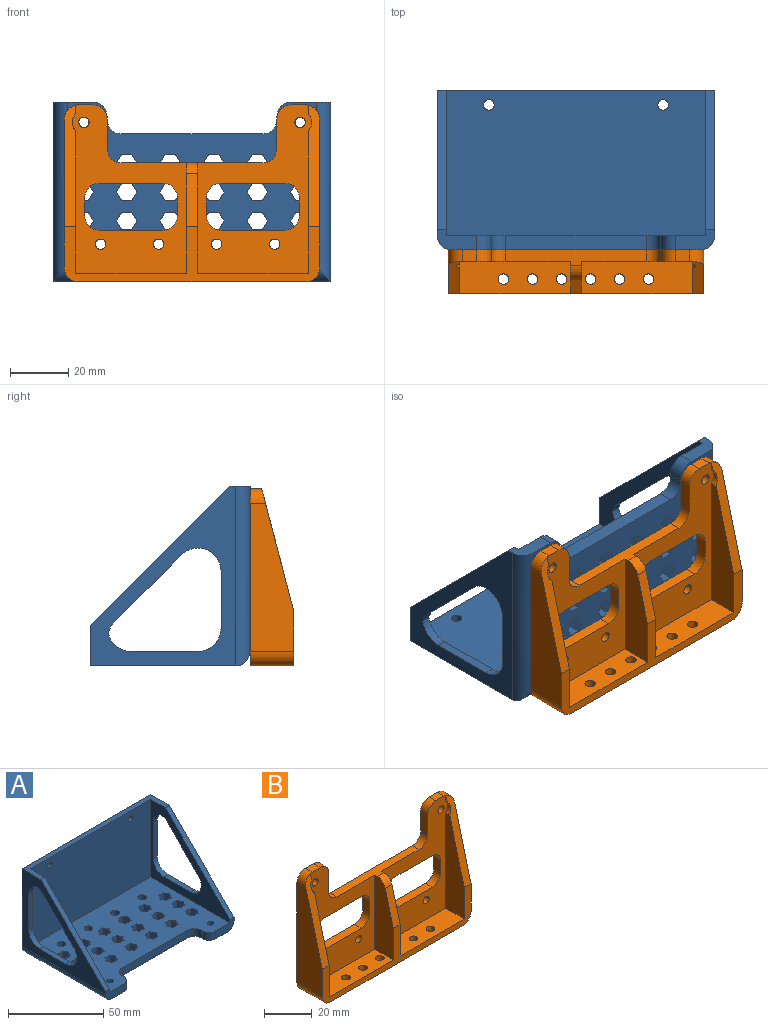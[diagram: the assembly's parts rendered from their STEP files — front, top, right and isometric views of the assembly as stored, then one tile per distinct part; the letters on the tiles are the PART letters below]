
ASSEMBLY  parts=2 mates=1
PART A: 153 faces, bbox 95.5x62x55 mm
  f0: plane 62x50mm, normal (1,0,0), area 986mm2, adj f6,f7,f15,f20,f28,f139,f140,f141
  f1: plane 62x50mm, normal (-1,0,0), area 986mm2, adj f7,f8,f15,f21,f30,f142,f143,f144
  f2: plane 59x50mm, normal (1,0,0), area 836mm2, adj f8,f12,f14,f15,f21,f142,f143,f144
  f3: plane 59x50mm, normal (-1,0,0), area 836mm2, adj f6,f12,f14,f15,f20,f139,f140,f141
  f4: plane 48.5x5mm, normal (0,-1,0), area 242.5mm2, adj f12,f13,f22,f23
  f5: plane 5x1mm, normal (-1,0,0), area 5mm2, adj f12,f13,f22,f25
  f6: plane 13.5x7mm, normal (0,-1,0), area 68.1mm2, adj f0,f3,f12,f13,f20,f25,f28
  f7: plane 95.5x50mm, normal (0,1,0), area 4754.6mm2, adj f0,f1,f15,f26,f27,f29
  f8: plane 13.5x7mm, normal (0,-1,0), area 68.1mm2, adj f1,f2,f12,f13,f21,f24,f30
  f9: cylinder r=1.75mm len=5mm, axis (0,0,-1), area 55mm2, adj f12,f13
  f10: plane 5x1mm, normal (1,0,0), area 5mm2, adj f12,f13,f23,f24
  f11: cylinder r=1.75mm len=5mm, axis (0,0,-1), area 55mm2, adj f12,f13
  f12: plane 89.5x59mm, normal (0,0,1), area 3993mm2, adj f2,f3,f4,f5,f6,f8,f9,f10
  f13: plane 85.5x57mm, normal (0,0,-1), area 3586mm2, adj f4,f5,f6,f8,f9,f10,f11,f16
  f14: plane 89.5x50mm, normal (0,-1,0), area 4454.6mm2, adj f2,f3,f12,f15,f26,f27
  f15: plane 95.5x14mm, normal (0,0,1), area 352.5mm2, adj f0,f1,f2,f3,f7,f14,f20,f21
  f16: cylinder r=2.25mm len=5mm, axis (0,0,-1), area 70.7mm2, adj f12,f13
  f17: cylinder r=2.25mm len=5mm, axis (0,0,-1), area 70.7mm2, adj f12,f13
  f18: cylinder r=2.25mm len=5mm, axis (0,0,-1), area 70.7mm2, adj f12,f13
  f19: cylinder r=2.25mm len=5mm, axis (0,0,-1), area 70.7mm2, adj f12,f13
  f20: plane 48x48mm, normal (0,-0.71,0.71), area 203.6mm2, adj f0,f3,f6,f15
  f21: plane 48x48mm, normal (0,-0.71,0.71), area 203.6mm2, adj f1,f2,f8,f15
  f22: cylinder r=5mm len=5mm, axis (0,0,-1), area 39.3mm2, adj f4,f5,f12,f13
  f23: cylinder r=5mm len=5mm, axis (0,0,1), area 39.3mm2, adj f4,f10,f12,f13
  f24: cylinder r=5mm len=5mm, axis (0,0,1), area 39.3mm2, adj f8,f10,f12,f13
  f25: cylinder r=5mm len=5mm, axis (0,0,1), area 39.3mm2, adj f5,f6,f12,f13
  f26: cylinder r=1.8mm len=3.6mm, axis (0,-1,0), area 33.9mm2, adj f7,f14
  f27: cylinder r=1.8mm len=3.6mm, axis (0,-1,0), area 33.9mm2, adj f7,f14
  f28: cylinder r=5mm len=62mm, axis (0,1,0), area 472.7mm2, adj f0,f6,f13,f29
  f29: cylinder r=5mm len=95.5mm, axis (-1,0,0), area 721.5mm2, adj f7,f13,f28,f30
  f30: cylinder r=5mm len=62mm, axis (0,-1,0), area 472.7mm2, adj f1,f8,f13,f29
  f31: plane 5x3mm, normal (0.87,-0.5,0), area 17.3mm2, adj f12,f13,f32,f36
  f32: plane 5x3mm, normal (0.87,0.5,0), area 17.3mm2, adj f12,f13,f31,f33
  f33: plane 5x3.46mm, normal (0,1,0), area 17.3mm2, adj f12,f13,f32,f34
  f34: plane 5x3mm, normal (-0.87,0.5,0), area 17.3mm2, adj f12,f13,f33,f35
  f35: plane 5x3mm, normal (-0.87,-0.5,0), area 17.3mm2, adj f12,f13,f34,f36
  f36: plane 5x3.46mm, normal (0,-1,0), area 17.3mm2, adj f12,f13,f31,f35
  f37: plane 5x3mm, normal (0.87,0.5,0), area 17.3mm2, adj f12,f13,f38,f42
  f38: plane 5x3.46mm, normal (0,1,0), area 17.3mm2, adj f12,f13,f37,f39
  f39: plane 5x3mm, normal (-0.87,0.5,0), area 17.3mm2, adj f12,f13,f38,f40
  f40: plane 5x3mm, normal (-0.87,-0.5,0), area 17.3mm2, adj f12,f13,f39,f41
  f41: plane 5x3.46mm, normal (0,-1,0), area 17.3mm2, adj f12,f13,f40,f42
  f42: plane 5x3mm, normal (0.87,-0.5,0), area 17.3mm2, adj f12,f13,f37,f41
  f43: plane 5x3mm, normal (0.87,0.5,0), area 17.3mm2, adj f12,f13,f44,f48
  f44: plane 5x3.46mm, normal (0,1,0), area 17.3mm2, adj f12,f13,f43,f45
  f45: plane 5x3mm, normal (-0.87,0.5,0), area 17.3mm2, adj f12,f13,f44,f46
  f46: plane 5x3mm, normal (-0.87,-0.5,0), area 17.3mm2, adj f12,f13,f45,f47
  f47: plane 5x3.46mm, normal (0,-1,0), area 17.3mm2, adj f12,f13,f46,f48
  f48: plane 5x3mm, normal (0.87,-0.5,0), area 17.3mm2, adj f12,f13,f43,f47
  f49: plane 5x3mm, normal (0.87,0.5,0), area 17.3mm2, adj f12,f13,f50,f54
  f50: plane 5x3.46mm, normal (0,1,0), area 17.3mm2, adj f12,f13,f49,f51
  f51: plane 5x3mm, normal (-0.87,0.5,0), area 17.3mm2, adj f12,f13,f50,f52
  f52: plane 5x3mm, normal (-0.87,-0.5,0), area 17.3mm2, adj f12,f13,f51,f53
  f53: plane 5x3.46mm, normal (0,-1,0), area 17.3mm2, adj f12,f13,f52,f54
  f54: plane 5x3mm, normal (0.87,-0.5,0), area 17.3mm2, adj f12,f13,f49,f53
  f55: plane 5x3mm, normal (0.87,0.5,0), area 17.3mm2, adj f12,f13,f56,f60
  f56: plane 5x3.46mm, normal (0,1,0), area 17.3mm2, adj f12,f13,f55,f57
  f57: plane 5x3mm, normal (-0.87,0.5,0), area 17.3mm2, adj f12,f13,f56,f58
  f58: plane 5x3mm, normal (-0.87,-0.5,0), area 17.3mm2, adj f12,f13,f57,f59
  f59: plane 5x3.46mm, normal (0,-1,0), area 17.3mm2, adj f12,f13,f58,f60
  f60: plane 5x3mm, normal (0.87,-0.5,0), area 17.3mm2, adj f12,f13,f55,f59
  f61: plane 5x3mm, normal (0.87,0.5,0), area 17.3mm2, adj f12,f13,f62,f66
  f62: plane 5x3.46mm, normal (0,1,0), area 17.3mm2, adj f12,f13,f61,f63
  f63: plane 5x3mm, normal (-0.87,0.5,0), area 17.3mm2, adj f12,f13,f62,f64
  f64: plane 5x3mm, normal (-0.87,-0.5,0), area 17.3mm2, adj f12,f13,f63,f65
  f65: plane 5x3.46mm, normal (0,-1,0), area 17.3mm2, adj f12,f13,f64,f66
  f66: plane 5x3mm, normal (0.87,-0.5,0), area 17.3mm2, adj f12,f13,f61,f65
  f67: plane 5x3mm, normal (0.87,0.5,0), area 17.3mm2, adj f12,f13,f68,f72
  f68: plane 5x3.46mm, normal (0,1,0), area 17.3mm2, adj f12,f13,f67,f69
  f69: plane 5x3mm, normal (-0.87,0.5,0), area 17.3mm2, adj f12,f13,f68,f70
  f70: plane 5x3mm, normal (-0.87,-0.5,0), area 17.3mm2, adj f12,f13,f69,f71
  f71: plane 5x3.46mm, normal (0,-1,0), area 17.3mm2, adj f12,f13,f70,f72
  f72: plane 5x3mm, normal (0.87,-0.5,0), area 17.3mm2, adj f12,f13,f67,f71
  f73: plane 5x3mm, normal (0.87,0.5,0), area 17.3mm2, adj f12,f13,f74,f78
  f74: plane 5x3.46mm, normal (0,1,0), area 17.3mm2, adj f12,f13,f73,f75
  f75: plane 5x3mm, normal (-0.87,0.5,0), area 17.3mm2, adj f12,f13,f74,f76
  f76: plane 5x3mm, normal (-0.87,-0.5,0), area 17.3mm2, adj f12,f13,f75,f77
  f77: plane 5x3.46mm, normal (0,-1,0), area 17.3mm2, adj f12,f13,f76,f78
  f78: plane 5x3mm, normal (0.87,-0.5,0), area 17.3mm2, adj f12,f13,f73,f77
  f79: plane 5x3mm, normal (0.87,0.5,0), area 17.3mm2, adj f12,f13,f80,f84
  f80: plane 5x3.46mm, normal (0,1,0), area 17.3mm2, adj f12,f13,f79,f81
  f81: plane 5x3mm, normal (-0.87,0.5,0), area 17.3mm2, adj f12,f13,f80,f82
  f82: plane 5x3mm, normal (-0.87,-0.5,0), area 17.3mm2, adj f12,f13,f81,f83
  f83: plane 5x3.46mm, normal (0,-1,0), area 17.3mm2, adj f12,f13,f82,f84
  f84: plane 5x3mm, normal (0.87,-0.5,0), area 17.3mm2, adj f12,f13,f79,f83
  f85: plane 5x3mm, normal (0.87,0.5,0), area 17.3mm2, adj f12,f13,f86,f90
  f86: plane 5x3.46mm, normal (0,1,0), area 17.3mm2, adj f12,f13,f85,f87
  f87: plane 5x3mm, normal (-0.87,0.5,0), area 17.3mm2, adj f12,f13,f86,f88
  f88: plane 5x3mm, normal (-0.87,-0.5,0), area 17.3mm2, adj f12,f13,f87,f89
  f89: plane 5x3.46mm, normal (0,-1,0), area 17.3mm2, adj f12,f13,f88,f90
  f90: plane 5x3mm, normal (0.87,-0.5,0), area 17.3mm2, adj f12,f13,f85,f89
  f91: plane 5x3mm, normal (0.87,0.5,0), area 17.3mm2, adj f12,f13,f92,f96
  f92: plane 5x3.46mm, normal (0,1,0), area 17.3mm2, adj f12,f13,f91,f93
  f93: plane 5x3mm, normal (-0.87,0.5,0), area 17.3mm2, adj f12,f13,f92,f94
  f94: plane 5x3mm, normal (-0.87,-0.5,0), area 17.3mm2, adj f12,f13,f93,f95
  f95: plane 5x3.46mm, normal (0,-1,0), area 17.3mm2, adj f12,f13,f94,f96
  f96: plane 5x3mm, normal (0.87,-0.5,0), area 17.3mm2, adj f12,f13,f91,f95
  f97: plane 5x3mm, normal (0.87,0.5,0), area 17.3mm2, adj f12,f13,f98,f102
  f98: plane 5x3.46mm, normal (0,1,0), area 17.3mm2, adj f12,f13,f97,f99
  f99: plane 5x3mm, normal (-0.87,0.5,0), area 17.3mm2, adj f12,f13,f98,f100
  f100: plane 5x3mm, normal (-0.87,-0.5,0), area 17.3mm2, adj f12,f13,f99,f101
  f101: plane 5x3.46mm, normal (0,-1,0), area 17.3mm2, adj f12,f13,f100,f102
  f102: plane 5x3mm, normal (0.87,-0.5,0), area 17.3mm2, adj f12,f13,f97,f101
  f103: plane 5x3mm, normal (0.87,0.5,0), area 17.3mm2, adj f12,f13,f104,f108
  f104: plane 5x3.46mm, normal (0,1,0), area 17.3mm2, adj f12,f13,f103,f105
  f105: plane 5x3mm, normal (-0.87,0.5,0), area 17.3mm2, adj f12,f13,f104,f106
  f106: plane 5x3mm, normal (-0.87,-0.5,0), area 17.3mm2, adj f12,f13,f105,f107
  f107: plane 5x3.46mm, normal (0,-1,0), area 17.3mm2, adj f12,f13,f106,f108
  f108: plane 5x3mm, normal (0.87,-0.5,0), area 17.3mm2, adj f12,f13,f103,f107
  f109: plane 5x3mm, normal (0.87,0.5,0), area 17.3mm2, adj f12,f13,f110,f114
  f110: plane 5x3.46mm, normal (0,1,0), area 17.3mm2, adj f12,f13,f109,f111
  f111: plane 5x3mm, normal (-0.87,0.5,0), area 17.3mm2, adj f12,f13,f110,f112
  f112: plane 5x3mm, normal (-0.87,-0.5,0), area 17.3mm2, adj f12,f13,f111,f113
  f113: plane 5x3.46mm, normal (0,-1,0), area 17.3mm2, adj f12,f13,f112,f114
  f114: plane 5x3mm, normal (0.87,-0.5,0), area 17.3mm2, adj f12,f13,f109,f113
  f115: plane 5x3mm, normal (0.87,0.5,0), area 17.3mm2, adj f12,f13,f116,f120
  f116: plane 5x3.46mm, normal (0,1,0), area 17.3mm2, adj f12,f13,f115,f117
  f117: plane 5x3mm, normal (-0.87,0.5,0), area 17.3mm2, adj f12,f13,f116,f118
  f118: plane 5x3mm, normal (-0.87,-0.5,0), area 17.3mm2, adj f12,f13,f117,f119
  f119: plane 5x3.46mm, normal (0,-1,0), area 17.3mm2, adj f12,f13,f118,f120
  f120: plane 5x3mm, normal (0.87,-0.5,0), area 17.3mm2, adj f12,f13,f115,f119
  f121: plane 5x3mm, normal (0.87,0.5,0), area 17.3mm2, adj f12,f13,f122,f126
  f122: plane 5x3.46mm, normal (0,1,0), area 17.3mm2, adj f12,f13,f121,f123
  f123: plane 5x3mm, normal (-0.87,0.5,0), area 17.3mm2, adj f12,f13,f122,f124
  f124: plane 5x3mm, normal (-0.87,-0.5,0), area 17.3mm2, adj f12,f13,f123,f125
  f125: plane 5x3.46mm, normal (0,-1,0), area 17.3mm2, adj f12,f13,f124,f126
  f126: plane 5x3mm, normal (0.87,-0.5,0), area 17.3mm2, adj f12,f13,f121,f125
  f127: plane 5x3mm, normal (0.87,0.5,0), area 17.3mm2, adj f12,f13,f128,f132
  f128: plane 5x3.46mm, normal (0,1,0), area 17.3mm2, adj f12,f13,f127,f129
  f129: plane 5x3mm, normal (-0.87,0.5,0), area 17.3mm2, adj f12,f13,f128,f130
  f130: plane 5x3mm, normal (-0.87,-0.5,0), area 17.3mm2, adj f12,f13,f129,f131
  f131: plane 5x3.46mm, normal (0,-1,0), area 17.3mm2, adj f12,f13,f130,f132
  f132: plane 5x3mm, normal (0.87,-0.5,0), area 17.3mm2, adj f12,f13,f127,f131
  f133: plane 5x3mm, normal (0.87,0.5,0), area 17.3mm2, adj f12,f13,f134,f138
  f134: plane 5x3.46mm, normal (0,1,0), area 17.3mm2, adj f12,f13,f133,f135
  f135: plane 5x3mm, normal (-0.87,0.5,0), area 17.3mm2, adj f12,f13,f134,f136
  f136: plane 5x3mm, normal (-0.87,-0.5,0), area 17.3mm2, adj f12,f13,f135,f137
  f137: plane 5x3.46mm, normal (0,-1,0), area 17.3mm2, adj f12,f13,f136,f138
  f138: plane 5x3mm, normal (0.87,-0.5,0), area 17.3mm2, adj f12,f13,f133,f137
  f139: plane 23x3mm, normal (0,-1,0), area 69mm2, adj f0,f3,f145,f148
  f140: plane 19.62x3mm, normal (0,0,1), area 58.8mm2, adj f0,f3,f147,f148
  f141: plane 23x23mm, normal (0,0.71,-0.71), area 97.6mm2, adj f0,f3,f146,f147
  f142: plane 23x23mm, normal (0,0.71,-0.71), area 97.6mm2, adj f1,f2,f150,f151
  f143: plane 19.62x3mm, normal (0,0,1), area 58.8mm2, adj f1,f2,f151,f152
  f144: plane 23x3mm, normal (0,-1,0), area 69mm2, adj f1,f2,f149,f152
  f145: cylinder r=8mm len=7.82mm, axis (-1,0,0), area 32.6mm2, adj f0,f3,f139,f146
  f146: cylinder r=8mm len=3.96mm, axis (-1,0,0), area 13.7mm2, adj f0,f3,f141,f145
  f147: cylinder r=8mm len=13.66mm, axis (-1,0,0), area 56.5mm2, adj f0,f3,f140,f141
  f148: cylinder r=8mm len=8mm, axis (-1,0,0), area 37.7mm2, adj f0,f3,f139,f140
  f149: cylinder r=8mm len=7.82mm, axis (-1,0,0), area 32.6mm2, adj f1,f2,f144,f150
  f150: cylinder r=8mm len=3.96mm, axis (-1,0,0), area 13.7mm2, adj f1,f2,f142,f149
  f151: cylinder r=8mm len=13.66mm, axis (-1,0,0), area 56.5mm2, adj f1,f2,f142,f143
  f152: cylinder r=8mm len=8mm, axis (-1,0,0), area 37.7mm2, adj f1,f2,f143,f144
PART B: 62 faces, bbox 88x15x61 mm
  f0: plane 58x39.25mm, normal (0,-1,0), area 1136.5mm2, adj f4,f8,f10,f14,f24,f26,f27,f30
  f1: plane 88x61mm, normal (0,1,0), area 3121.6mm2, adj f11,f12,f16,f23,f24,f25,f26,f27
  f2: plane 58x39.25mm, normal (0,-1,0), area 1136.5mm2, adj f5,f9,f13,f15,f16,f25,f28,f29
  f3: plane 18.21x4.78mm, normal (0,-0.97,0.25), area 75.3mm2, adj f4,f5,f35,f41
  f4: plane 38x11mm, normal (-1,0,0), area 352mm2, adj f0,f3,f10,f35,f40,f41
  f5: plane 38x11mm, normal (1,0,0), area 352mm2, adj f2,f3,f13,f35,f40,f41
  f6: plane 41.84x10.97mm, normal (0,-0.97,0.25), area 162.7mm2, adj f9,f12,f15,f29,f35,f36
  f7: plane 41.84x10.97mm, normal (0,-0.97,0.25), area 162.7mm2, adj f8,f11,f14,f30,f35,f37
  f8: plane 49.1x11mm, normal (1,0,0), area 396.9mm2, adj f0,f7,f10,f30,f35
  f9: plane 49.1x11mm, normal (-1,0,0), area 396.9mm2, adj f2,f6,f13,f29,f35
  f10: plane 38x11mm, normal (0,0,1), area 387.5mm2, adj f0,f4,f8,f17,f20,f21,f35
  f11: plane 51x15mm, normal (-1,0,0), area 586.1mm2, adj f1,f7,f35,f37,f39
  f12: plane 51x15mm, normal (1,0,0), area 586.1mm2, adj f1,f6,f35,f36,f38
  f13: plane 38x11mm, normal (0,0,1), area 387.5mm2, adj f2,f5,f9,f18,f19,f22,f35
  f14: plane 2.99x0.81mm, normal (1,0,0), area 1.3mm2, adj f0,f7,f30,f37
  f15: plane 2.99x0.81mm, normal (-1,0,0), area 1.3mm2, adj f2,f6,f29,f36
  f16: plane 4.75x4mm, normal (0,0,1), area 19mm2, adj f1,f2,f36,f44
  f17: cylinder r=1.8mm len=3.6mm, axis (0,0,-1), area 33.9mm2, adj f10,f23
  f18: cylinder r=1.8mm len=3.6mm, axis (0,0,-1), area 33.9mm2, adj f13,f23
  f19: cylinder r=1.8mm len=3.6mm, axis (0,0,-1), area 33.9mm2, adj f13,f23
  f20: cylinder r=1.8mm len=3.6mm, axis (0,0,-1), area 33.9mm2, adj f10,f23
  f21: cylinder r=1.8mm len=3.6mm, axis (0,0,-1), area 33.9mm2, adj f10,f23
  f22: cylinder r=1.8mm len=3.6mm, axis (0,0,-1), area 33.9mm2, adj f13,f23
  f23: plane 78x15mm, normal (0,0,-1), area 1108.9mm2, adj f1,f17,f18,f19,f20,f21,f22,f35
  f24: plane 4.75x4mm, normal (0,0,1), area 19mm2, adj f0,f1,f37,f45
  f25: cylinder r=1.8mm len=4mm, axis (0,1,0), area 45.2mm2, adj f1,f2
  f26: cylinder r=1.8mm len=4mm, axis (0,1,0), area 45.2mm2, adj f0,f1
  f27: plane 10x4mm, normal (1,0,0), area 40mm2, adj f0,f1,f43,f45
  f28: plane 10x4mm, normal (-1,0,0), area 40mm2, adj f1,f2,f42,f44
  f29: cylinder r=4mm len=5.81mm, axis (0,1,0), area 10.2mm2, adj f2,f6,f9,f15
  f30: cylinder r=4mm len=5.81mm, axis (0,1,0), area 10.2mm2, adj f0,f7,f8,f14
  f31: cylinder r=1.8mm len=4mm, axis (0,1,0), area 45.2mm2, adj f1,f2
  f32: cylinder r=1.8mm len=4mm, axis (0,1,0), area 45.2mm2, adj f1,f2
  f33: cylinder r=1.8mm len=4mm, axis (0,1,0), area 45.2mm2, adj f0,f1
  f34: cylinder r=1.8mm len=4mm, axis (0,1,0), area 45.2mm2, adj f0,f1
  f35: plane 88x19.06mm, normal (0,-1,0), area 446mm2, adj f3,f4,f5,f6,f7,f8,f9,f10
  f36: cylinder r=5mm len=5.31mm, axis (0,-1,0), area 35.1mm2, adj f1,f2,f6,f12,f15,f16
  f37: cylinder r=5mm len=5.31mm, axis (0,1,0), area 35.1mm2, adj f0,f1,f7,f11,f14,f24
  f38: cylinder r=5mm len=15mm, axis (0,1,0), area 117.8mm2, adj f1,f12,f23,f35
  f39: cylinder r=5mm len=15mm, axis (0,-1,0), area 117.8mm2, adj f1,f11,f23,f35
  f40: plane 48.5x5.39mm, normal (0,0,1), area 199.6mm2, adj f0,f1,f2,f4,f5,f41,f42,f43
  f41: cylinder r=5mm len=4.84mm, axis (-1,0,0), area 26.3mm2, adj f3,f4,f5,f40
  f42: cylinder r=5mm len=5mm, axis (0,-1,0), area 31.4mm2, adj f1,f2,f28,f40
  f43: cylinder r=5mm len=5mm, axis (0,1,0), area 31.4mm2, adj f0,f1,f27,f40
  f44: cylinder r=5mm len=5mm, axis (0,-1,0), area 31.4mm2, adj f1,f2,f16,f28
  f45: cylinder r=5mm len=5mm, axis (0,1,0), area 31.4mm2, adj f0,f1,f24,f27
  f46: plane 22x4mm, normal (0,0,-1), area 88mm2, adj f1,f2,f58,f61
  f47: plane 6.2x4mm, normal (1,0,0), area 24.8mm2, adj f1,f2,f58,f59
  f48: plane 22x4mm, normal (0,0,1), area 88mm2, adj f1,f2,f59,f60
  f49: plane 6.2x4mm, normal (-1,0,0), area 24.8mm2, adj f1,f2,f60,f61
  f50: plane 22x4mm, normal (0,0,-1), area 88mm2, adj f0,f1,f54,f57
  f51: plane 6.2x4mm, normal (1,0,0), area 24.8mm2, adj f0,f1,f54,f55
  f52: plane 22x4mm, normal (0,0,1), area 88mm2, adj f0,f1,f55,f56
  f53: plane 6.2x4mm, normal (-1,0,0), area 24.8mm2, adj f0,f1,f56,f57
  f54: cylinder r=5mm len=5mm, axis (0,-1,0), area 31.4mm2, adj f0,f1,f50,f51
  f55: cylinder r=5mm len=5mm, axis (0,1,0), area 31.4mm2, adj f0,f1,f51,f52
  f56: cylinder r=5mm len=5mm, axis (0,-1,0), area 31.4mm2, adj f0,f1,f52,f53
  f57: cylinder r=5mm len=5mm, axis (0,1,0), area 31.4mm2, adj f0,f1,f50,f53
  f58: cylinder r=5mm len=5mm, axis (0,-1,0), area 31.4mm2, adj f1,f2,f46,f47
  f59: cylinder r=5mm len=5mm, axis (0,1,0), area 31.4mm2, adj f1,f2,f47,f48
  f60: cylinder r=5mm len=5mm, axis (0,-1,0), area 31.4mm2, adj f1,f2,f48,f49
  f61: cylinder r=5mm len=5mm, axis (0,1,0), area 31.4mm2, adj f1,f2,f46,f49
PLACE A rot(axis=(-1,0,0),90deg) t=(56.41,37.92,102.97)mm
PLACE B t=(56.41,27.92,47.97)mm
MATE cylindrical B.f25 <-> A.f11  axis (0,1,0) through (93.66,37.92,102.97)mm
